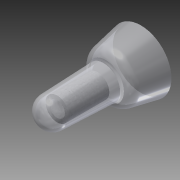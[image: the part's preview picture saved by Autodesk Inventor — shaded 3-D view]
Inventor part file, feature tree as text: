
AUTODESK INVENTOR PART (.ipt)
format: ipt  version: 2014 (Build 180170000, 170)  size: 297,984 bytes
history: native  units: in
note: dims shown in document units (in); Inventor stores cm internally (conversion verified against a paired STEP export)
features: fillet x5, sketch x4, projected_geometry x3, extrude x2, revolve x2, mirror x1, shell x1, plane x1
ambient origin geometry x8: Origin, YZ Plane, XZ Plane, XY Plane, X Axis, Y Axis, Z Axis, Center Point
bodies: Solid1 (feature_tree), Solid2 (feature_tree), Solid3 (feature_tree)
feature tree (19):
  extrude  "Extrusion1"  Depth=0.229in TaperAngle=0.0deg
  extrude  "Extrusion2"  Depth=0.01in TaperAngle=0.0deg
  fillet  "Fillet1"  Radius=0.01in
  mirror  "Mirror1"
  shell  "Shell1"  Thickness=0.0175in
  revolve  "Revolution1"  [1 undecoded]
  plane  "Work Plane1"
  revolve  "Revolution2"  [1 undecoded]
  fillet  "Fillet7"  Radius=0.02in
  fillet  "Fillet8"  Radius=0.02in
  fillet  "Fillet9"  Radius=0.02in
  fillet  "Fillet10"  Radius=0.02in
  sketch  "Sketch1"  dims[d0=0.219in d1=0.229in d2=0.0in]
  sketch  "Sketch2"  dims[d3=0.236in d4=0.068in d5=0.0in d6=0.01in d7=0.0175in]
  projected_geometry  "Projected Loop1"
  sketch  "Sketch3"  dims[d8=0.031in d9=0.031in]
  sketch  "Sketch8"  dims[d10=90.0deg d11=0.082in d14=0.339in d15=0.073in d43=0.02in d45=0.02in d46=0.02in d51=0.02in d52=90.0deg d53=0.1in d54=0.02in d55=0.1in d56=0.02in]
  projected_geometry  "Project Cut Edges1"
  projected_geometry  "Project Cut Edges3"
note: 2 required parameter values undecoded (feature->parameter linkage not recoverable at this tier; creation-order binding heuristic only, values carry confidence <= 0.55)
